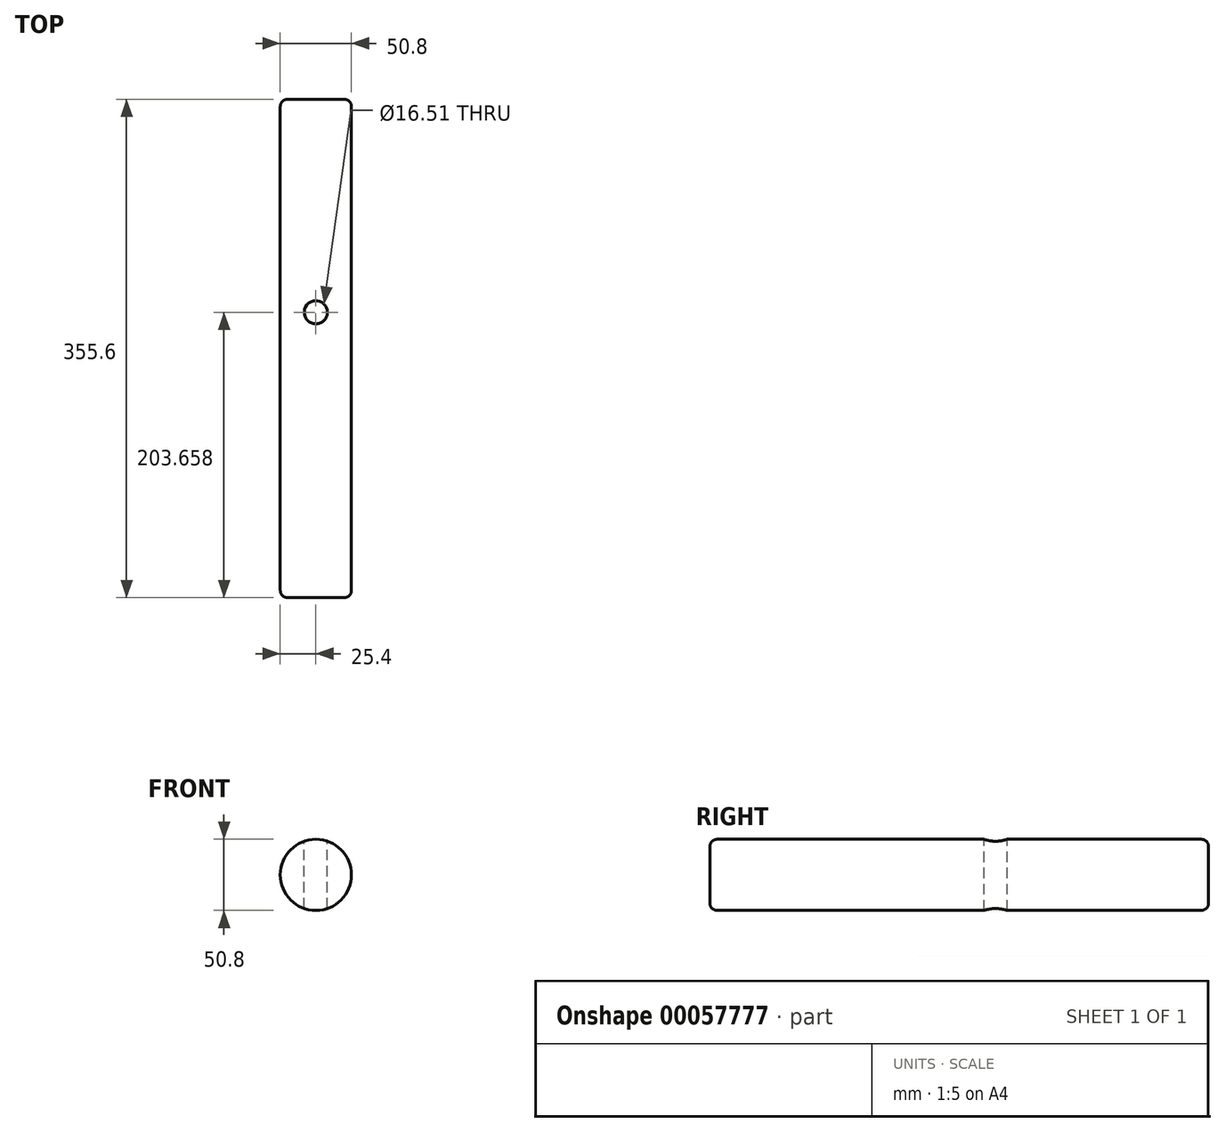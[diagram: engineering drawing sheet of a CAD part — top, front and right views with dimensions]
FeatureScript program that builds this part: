
annotation { "Feature Type Name" : "Feature", "Feature Type Description" : "" }
export const myFeature = defineFeature(function(context is Context, id is Id, definition is map)
    precondition{}
    {
        {
            var Q0;
            Q0=qCreatedBy(makeId("Front.planeOp"),FACE);
            var sketch = newSketch(context, id + "F0", { "sketchPlane" : qUnion([Q0])});
            skCircle(sketch, "E0", {"center": v(0, 0) * mm, "radius": 25.4 * mm});
            skSolve(sketch);
        }
        {
            var Q0;
            Q0 = qSketchRegion(id + "F0", true);
            extrude(context, id + "F1", {"entities" : qUnion([Q0]), "depth" : 355.6 * mm});
        }
        {
            var Q0;
            Q0=makeQuery(id+"F1.opExtrude","CAP_EDGE",EDGE,{"disambiguationData":[OSD([sQuery(id+"F0.wireOp",EDGE,"E0")])],"isStart":false});
            fillet(context, id + "F2", {"entities" : qUnion([Q0]), "radius" : 5.08 * mm, "tangentPropagation" : true, "allowEdgeOverflow" : false});
        }
        {
            var Q0;
            Q0=makeQuery(id+"F1.opExtrude","CAP_EDGE",EDGE,{"disambiguationData":[OSD([sQuery(id+"F0.wireOp",EDGE,"E0")])],"isStart":true});
            fillet(context, id + "F3", {"entities" : qUnion([Q0]), "radius" : 5.08 * mm, "tangentPropagation" : true, "allowEdgeOverflow" : false});
        }
        {
            var Q0;
            Q0=qCreatedBy(makeId("Top.planeOp"),FACE);
            var sketch = newSketch(context, id + "F4", { "sketchPlane" : qUnion([Q0])});
            skCircle(sketch, "E1", {"center": v(0, -151.94) * mm, "radius": 8.25 * mm});
            skSolve(sketch);
        }
        {
            var Q0;
            Q0 = qSketchRegion(id + "F4", true);
            extrude(context, id + "F5", {"entities" : qUnion([Q0]), "operationType" : NewBodyOperationType.REMOVE, "endBound" : BoundingType.SYMMETRIC, "oppositeDirection" : true, "depth" : 177.8 * mm});
        }
    });
